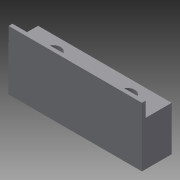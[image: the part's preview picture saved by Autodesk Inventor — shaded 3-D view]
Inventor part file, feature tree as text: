
AUTODESK INVENTOR PART (.ipt)
format: ipt  version: 2015 (Build 190159000, 159)  size: 88,576 bytes
history: native  units: mm
features: extrude x2, sketch x2
ambient origin geometry x8: Origin, YZ Plane, XZ Plane, XY Plane, X Axis, Y Axis, Z Axis, Center Point
bodies: Solid1 (feature_tree)
feature tree (4):
  extrude  "Extrusion1"  Depth=5.2mm
  extrude  "Extrusion2"  Depth=5.0mm
  sketch  "Sketch1"  dims[d0=5.2mm d1=5.2mm]
  sketch  "Sketch2"  dims[d2=10.0mm d3=5.0mm d4=5.0mm d5=10.0mm d6=45.0mm d7=10.0mm d8=25.0mm d9=15.0mm d10=0.0mm d11=5.0mm d12=0.0mm]
